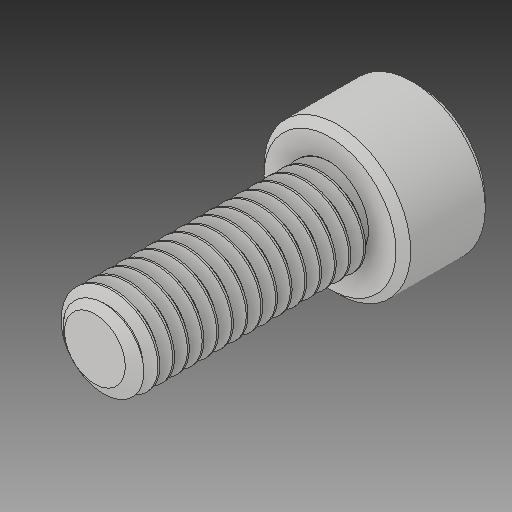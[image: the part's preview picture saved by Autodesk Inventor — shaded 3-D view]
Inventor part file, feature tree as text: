
AUTODESK INVENTOR PART (.ipt)
format: ipt  version: 2018.2 (Build 222227000, 227)  size: 809,984 bytes
history: native  units: in
note: dims shown in document units (in); Inventor stores cm internally (conversion verified against a paired STEP export)
features: chamfer x1
ambient origin geometry x8: Origin, YZ Plane, XZ Plane, XY Plane, X Axis, Y Axis, Z Axis, Center Point
bodies: Solid1 (feature_tree)
feature tree (1):
  chamfer  "Chamfer1"  [1 undecoded]
note: 1 required parameter value undecoded (feature->parameter linkage not recoverable at this tier; creation-order binding heuristic only, values carry confidence <= 0.55)
